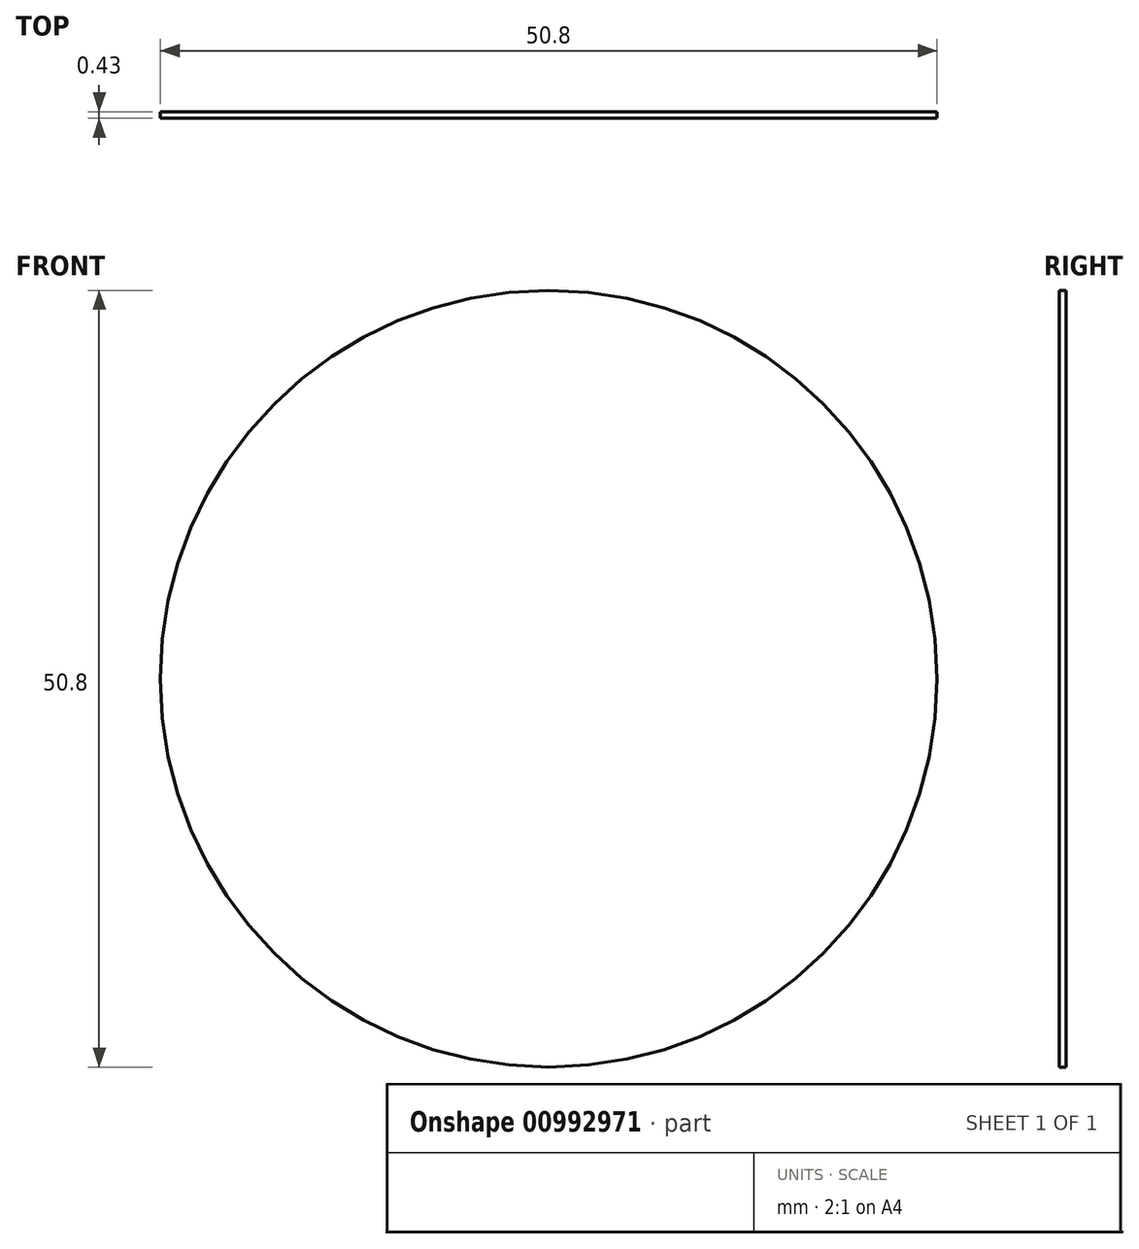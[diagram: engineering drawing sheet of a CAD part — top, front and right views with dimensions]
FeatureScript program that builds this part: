
annotation { "Feature Type Name" : "Feature", "Feature Type Description" : "" }
export const myFeature = defineFeature(function(context is Context, id is Id, definition is map)
    precondition{}
    {
        {
            var Q0;
            Q0=qCreatedBy(makeId("Front.planeOp"),FACE);
            var sketch = newSketch(context, id + "F0", { "sketchPlane" : qUnion([Q0])});
            skCircle(sketch, "E0", {"center": v(0, 0) * mm, "radius": 25.4 * mm});
            skSolve(sketch);
        }
        {
            var Q0;
            Q0 = qSketchRegion(id + "F0", true);
            extrude(context, id + "F1", {"entities" : qUnion([Q0]), "depth" : .43 * mm, "offsetDistance" : 25 * mm});
        }
    });
